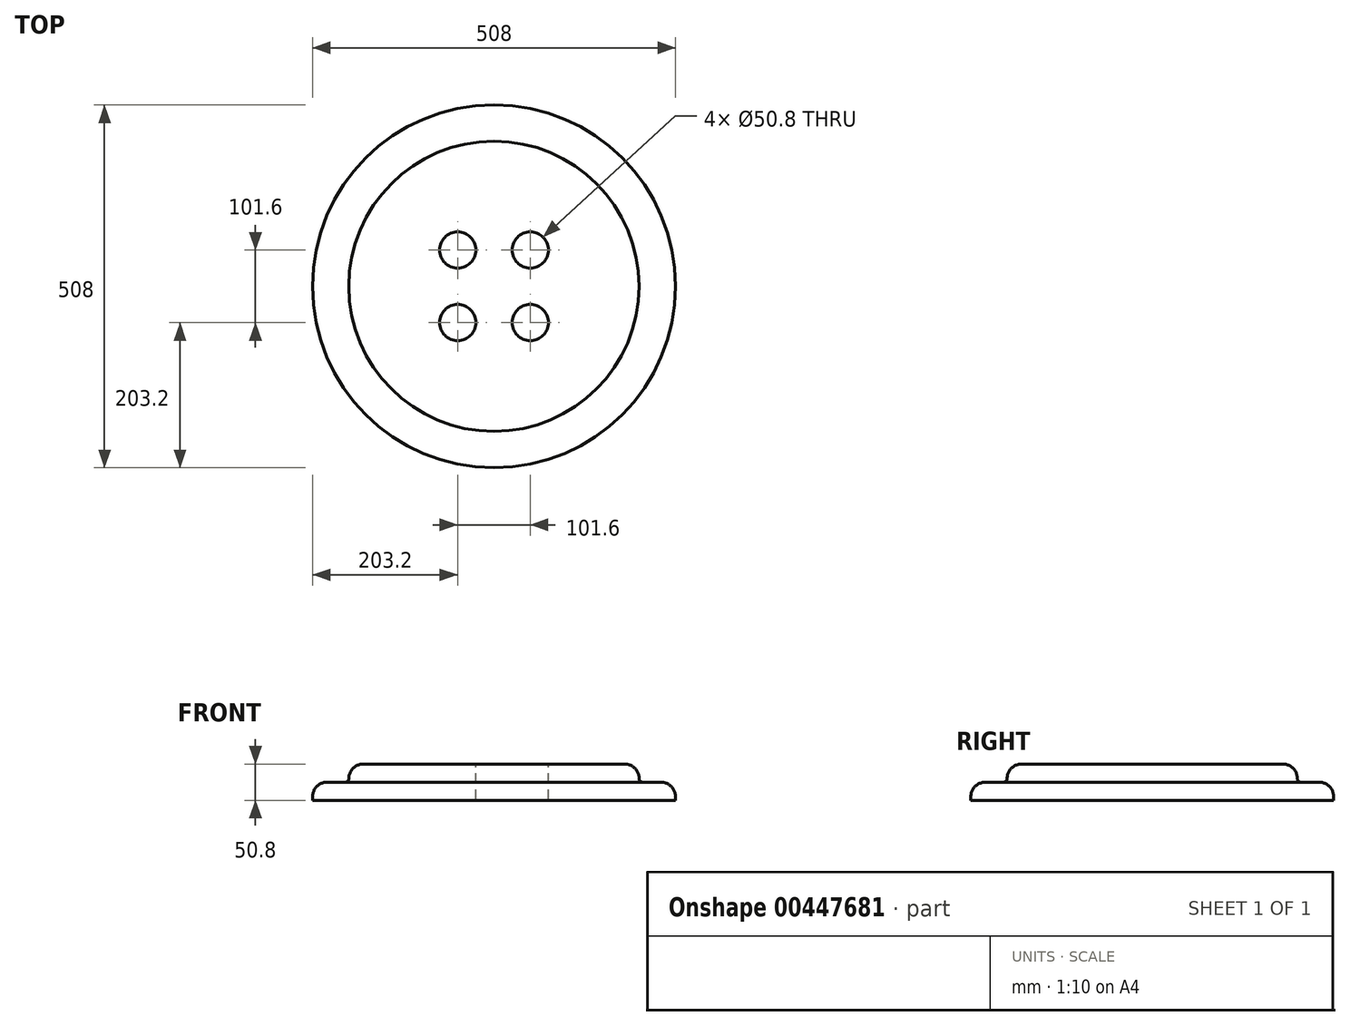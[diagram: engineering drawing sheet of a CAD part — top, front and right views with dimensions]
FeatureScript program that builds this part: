
annotation { "Feature Type Name" : "Feature", "Feature Type Description" : "" }
export const myFeature = defineFeature(function(context is Context, id is Id, definition is map)
    precondition{}
    {
        {
            var Q0;
            Q0=qCreatedBy(makeId("Front.planeOp"),FACE);
            var sketch = newSketch(context, id + "F0", { "sketchPlane" : qUnion([Q0])});
            skLineSegment(sketch, "E0", {"start": v(0, 103.55) * mm, "end": v(0, 0) * mm, "construction": true});
            skLineSegment(sketch, "E1", {"start": v(0, 0) * mm, "end": v(-254, 0) * mm});
            skLineSegment(sketch, "E2", {"start": v(-254, 0) * mm, "end": v(-254, 5.08) * mm});
            skLineSegment(sketch, "E3", {"start": v(-233.68, 25.4) * mm, "end": v(-208.28, 25.4) * mm});
            skLineSegment(sketch, "E4", {"start": v(-203.2, 30.48) * mm, "end": v(-203.2, 30.48) * mm});
            skLineSegment(sketch, "E5", {"start": v(-182.88, 50.8) * mm, "end": v(0, 50.8) * mm});
            skLineSegment(sketch, "E6", {"start": v(0, 50.8) * mm, "end": v(0, 0) * mm});
            skPoint(sketch, "E7.visualSharp", {"position": v(-254, 25.4) * mm});
            skArc(sketch, "E7.filletArc", {"start": v(-233.68, 25.4) * mm, "mid": v(-248.05, 19.45) * mm, "end": v(-254, 5.08) * mm});
            skPoint(sketch, "E8.visualSharp", {"position": v(-203.2, 25.4) * mm});
            skArc(sketch, "E8.filletArc", {"start": v(-208.28, 25.4) * mm, "mid": v(-204.69, 26.89) * mm, "end": v(-203.2, 30.48) * mm});
            skPoint(sketch, "E9.visualSharp", {"position": v(-203.2, 50.8) * mm});
            skArc(sketch, "E9.filletArc", {"start": v(-182.88, 50.8) * mm, "mid": v(-197.25, 44.85) * mm, "end": v(-203.2, 30.48) * mm});
            skSolve(sketch);
        }
        {
            var Q0;
            Q0=makeQuery(id+"F0.imprint","IMPRINT",FACE,{"disambiguationData":[TD([[makeQuery(id+"F0.imprint","IMPRINT",EDGE,{"derivedFrom":sQuery(id+"F0.wireOp",EDGE,"E1")}),-1.0]])]});
            var Q1;
            Q1=sQuery(id+"F0.wireOp",EDGE,"E6");
            revolve(context, id + "F1", {"entities" : qUnion([Q0]), "axis" : qUnion([Q1]), "revolveType" : RevolveType.FULL});
        }
        {
            var Q0;
            Q0=makeQuery(id+"F1.opRevolve","SWEPT_FACE",FACE,{"disambiguationData":[OSD([sQuery(id+"F0.wireOp",EDGE,"E5")])]});
            var sketch = newSketch(context, id + "F2", { "sketchPlane" : qUnion([Q0])});
            skCircle(sketch, "E10", {"center": v(-50.8, 50.8) * mm, "radius": 25.4 * mm});
            skLineSegment(sketch, "E11", {"start": v(-71.2, 0) * mm, "end": v(64.62, 0) * mm, "construction": true});
            skLineSegment(sketch, "E12", {"start": v(0, 67.31) * mm, "end": v(0, -64.32) * mm, "construction": true});
            skCircle(sketch, "E13.MirrorC", {"center": v(50.8, 50.8) * mm, "radius": 25.4 * mm});
            skCircle(sketch, "E14.MirrorC", {"center": v(-50.8, -50.8) * mm, "radius": 25.4 * mm});
            skCircle(sketch, "E15.MirrorC", {"center": v(50.8, -50.8) * mm, "radius": 25.4 * mm});
            skSolve(sketch);
        }
        {
            var Q0;
            Q0 = qSketchRegion(id + "F2", true);
            extrude(context, id + "F3", {"entities" : qUnion([Q0]), "operationType" : NewBodyOperationType.REMOVE, "oppositeDirection" : true, "depth" : 50.8 * mm});
        }
    });
